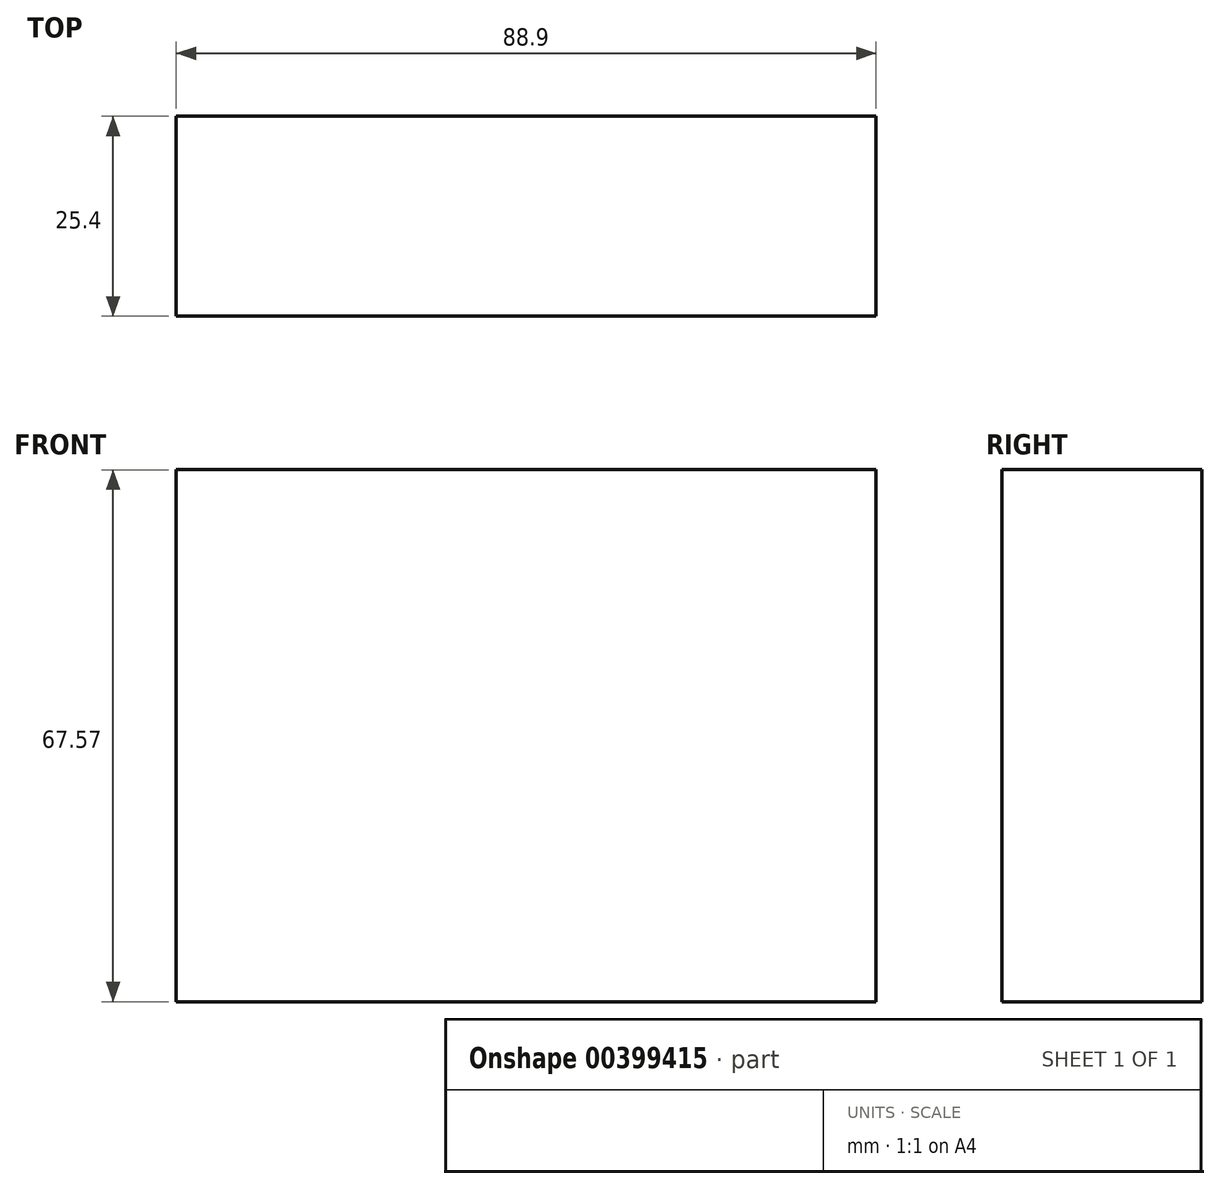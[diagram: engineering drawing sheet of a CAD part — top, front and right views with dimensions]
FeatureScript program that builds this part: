
annotation { "Feature Type Name" : "Feature", "Feature Type Description" : "" }
export const myFeature = defineFeature(function(context is Context, id is Id, definition is map)
    precondition{}
    {
        {
            var Q0;
            Q0=qCreatedBy(makeId("Front.planeOp"),FACE);
            var sketch = newSketch(context, id + "F0", { "sketchPlane" : qUnion([Q0])});
            skLineSegment(sketch, "E0.bottom", {"start": v(0, 0) * mm, "end": v(88.9, 0) * mm});
            skLineSegment(sketch, "E0.top", {"start": v(0, 67.57) * mm, "end": v(88.9, 67.57) * mm});
            skLineSegment(sketch, "E0.left", {"start": v(0, 0) * mm, "end": v(0, 67.57) * mm});
            skLineSegment(sketch, "E0.right", {"start": v(88.9, 0) * mm, "end": v(88.9, 67.57) * mm});
            skSolve(sketch);
        }
        {
            var Q0;
            Q0 = qSketchRegion(id + "F0", true);
            extrude(context, id + "F1", {"entities" : qUnion([Q0]), "depth" : 25.4 * mm});
        }
    });
